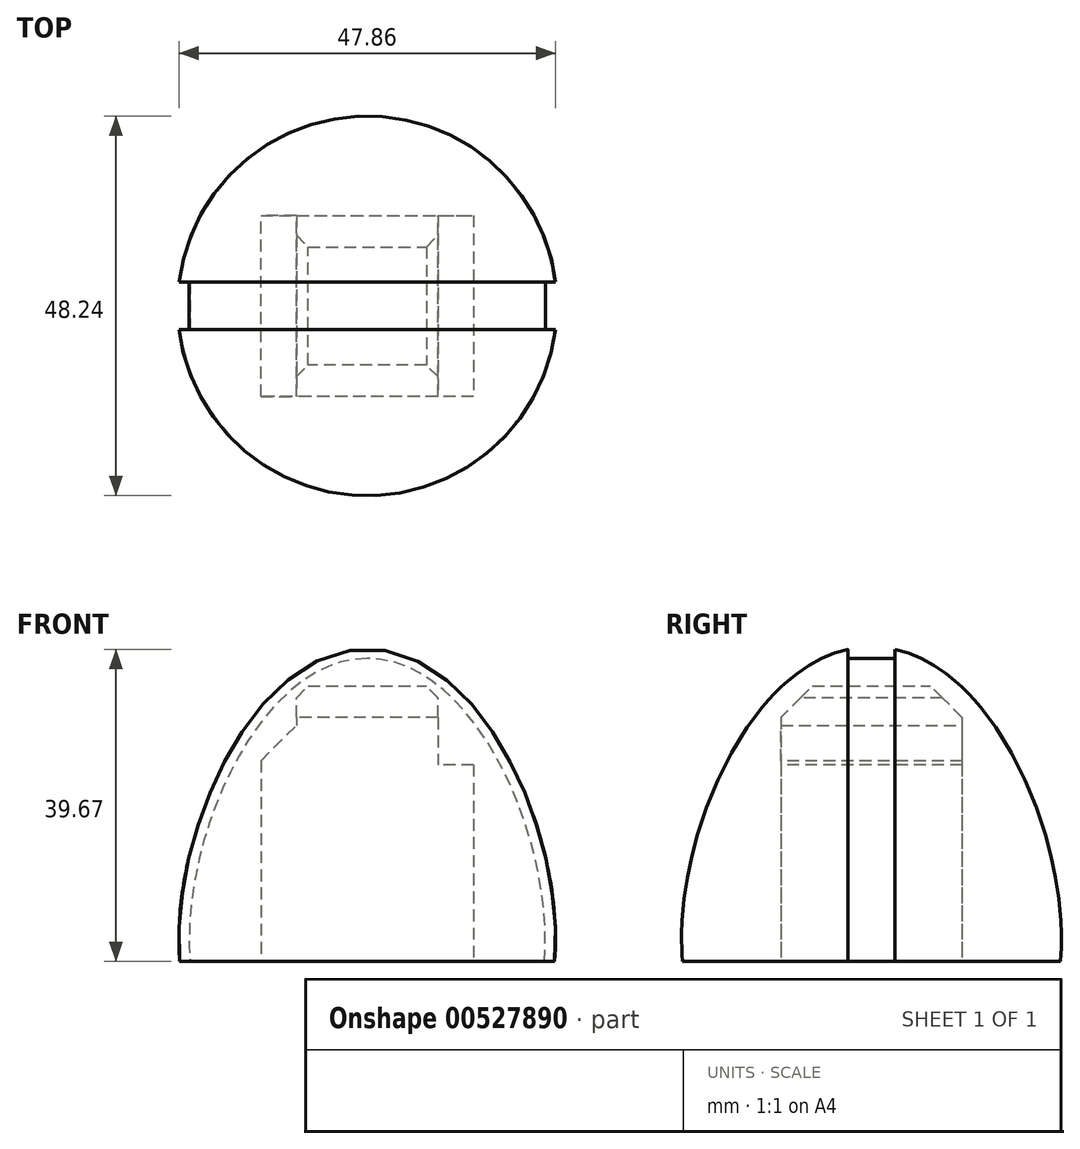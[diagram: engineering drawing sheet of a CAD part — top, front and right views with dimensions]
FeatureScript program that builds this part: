
annotation { "Feature Type Name" : "Feature", "Feature Type Description" : "" }
export const myFeature = defineFeature(function(context is Context, id is Id, definition is map)
    precondition{}
    {
        {
            var Q0;
            Q0=qCreatedBy(makeId("Front.planeOp"),FACE);
            var sketch = newSketch(context, id + "F0", { "sketchPlane" : qUnion([Q0])});
            skLineSegment(sketch, "E0", {"start": v(0, 0) * mm, "end": v(0, 60) * mm});
            skLineSegment(sketch, "E1", {"start": v(0, 0) * mm, "end": v(0, 20) * mm, "construction": true});
            skLineSegment(sketch, "E2", {"start": v(0, 20) * mm, "end": v(24, 20) * mm});
            skLineSegment(sketch, "E3", {"start": v(0, 60) * mm, "end": v(15, 60) * mm, "construction": true});
            skLineSegment(sketch, "E4", {"start": v(0, 0) * mm, "end": v(14, 0) * mm, "construction": true});
            skFitSpline(sketch, "E5", {"points": [v(0, 0) * mm, v(24, 20) * mm, v(0, 60) * mm], "startDerivative": vector(93.32, 0) * mm, "endDerivative": vector(-81.83, 0) * mm});
            skFitSpline(sketch, "E6.MirrorCS", {"points": [v(0, 0) * mm, v(-24, 20) * mm, v(0, 60) * mm], "startDerivative": vector(-93.32, 0) * mm, "endDerivative": vector(81.83, 0) * mm});
            skSolve(sketch);
        }
        {
            var Q0;
            {var subQ3=sQuery(id+"F0.wireOp",EDGE,"E2");Q0=makeQuery(id+"F0.imprint","IMPRINT",FACE,{"disambiguationData":[TD([[makeQuery(id+"F0.imprint","IMPRINT",EDGE,{"derivedFrom":subQ3}),1.0]])]});}
            var Q1;
            Q1=sQuery(id+"F0.wireOp",EDGE,"E0");
            revolve(context, id + "F1", {"entities" : qUnion([Q0]), "axis" : qUnion([Q1]), "revolveType" : RevolveType.FULL});
        }
        {
            var Q0;
            Q0=makeQuery(id+"F1.opRevolve","SWEPT_FACE",FACE,{"disambiguationData":[OSD([sQuery(id+"F0.wireOp",EDGE,"E2")])]});
            var sketch = newSketch(context, id + "F2", { "sketchPlane" : qUnion([Q0])});
            skLineSegment(sketch, "E7", {"start": v(0, 0) * mm, "end": v(13.5, 0) * mm});
            skLineSegment(sketch, "E8", {"start": v(13.5, 0) * mm, "end": v(13.5, 11.5) * mm});
            skLineSegment(sketch, "E9", {"start": v(13.5, 11.5) * mm, "end": v(-13.5, 11.5) * mm});
            skLineSegment(sketch, "E10", {"start": v(-13.5, 11.5) * mm, "end": v(-13.5, -11.5) * mm});
            skLineSegment(sketch, "E11", {"start": v(-13.5, -11.5) * mm, "end": v(13.5, -11.5) * mm});
            skLineSegment(sketch, "E12", {"start": v(13.5, -11.5) * mm, "end": v(13.5, 0) * mm});
            skSolve(sketch);
        }
        {
            var Q0;
            Q0=qSketchRegion(id+"F2",true);
            extrude(context, id + "F3", {"entities" : qUnion([Q0]), "operationType" : NewBodyOperationType.REMOVE, "oppositeDirection" : true, "depth" : 25 * mm});
        }
        {
            var Q0;
            Q0=makeQuery(id+"F3.boolean.opBoolean","COPY",FACE,{"derivedFrom":makeQuery(id+"F3.opExtrude","CAP_FACE",FACE,{"disambiguationData":[OSD([sQuery(id+"F2.wireOp",EDGE,"E8"),sQuery(id+"F2.wireOp",EDGE,"E9"),sQuery(id+"F2.wireOp",EDGE,"E10"),sQuery(id+"F2.wireOp",EDGE,"E11"),sQuery(id+"F2.wireOp",EDGE,"E12")])],"isStart":false})});
            var sketch = newSketch(context, id + "F4", { "sketchPlane" : qUnion([Q0])});
            skLineSegment(sketch, "E13", {"start": v(0, 0) * mm, "end": v(5, 0) * mm, "construction": true});
            skLineSegment(sketch, "E14", {"start": v(5, 0) * mm, "end": v(5, 5) * mm});
            skLineSegment(sketch, "E15", {"start": v(5, 5) * mm, "end": v(-5, 5) * mm});
            skLineSegment(sketch, "E16", {"start": v(-5, 5) * mm, "end": v(-5, -5) * mm});
            skLineSegment(sketch, "E17", {"start": v(-5, -5) * mm, "end": v(5, -5) * mm});
            skLineSegment(sketch, "E18", {"start": v(5, -5) * mm, "end": v(5, 0) * mm});
            skSolve(sketch);
        }
        {
            var Q0;
            Q0=qSketchRegion(id+"F4",true);
            extrude(context, id + "F5", {"entities" : qUnion([Q0]), "operationType" : NewBodyOperationType.REMOVE, "oppositeDirection" : true, "depth" : 10 * mm});
        }
        {
            var Q0;
            Q0=makeQuery(id+"F3.boolean.opBoolean","COPY",FACE,{"derivedFrom":makeQuery(id+"F3.opExtrude","CAP_FACE",FACE,{"disambiguationData":[OSD([sQuery(id+"F2.wireOp",EDGE,"E8"),sQuery(id+"F2.wireOp",EDGE,"E9"),sQuery(id+"F2.wireOp",EDGE,"E10"),sQuery(id+"F2.wireOp",EDGE,"E11"),sQuery(id+"F2.wireOp",EDGE,"E12")])],"isStart":false})});
            var sketch = newSketch(context, id + "F6", { "sketchPlane" : qUnion([Q0])});
            skLineSegment(sketch, "E19", {"start": v(0, 0) * mm, "end": v(9, 0) * mm, "construction": true});
            skLineSegment(sketch, "E20", {"start": v(9, 0) * mm, "end": v(9, 11.5) * mm});
            skLineSegment(sketch, "E21", {"start": v(9, 11.5) * mm, "end": v(-9, 11.5) * mm});
            skLineSegment(sketch, "E22", {"start": v(-9, 11.5) * mm, "end": v(-9, -11.5) * mm});
            skLineSegment(sketch, "E23", {"start": v(-9, -11.5) * mm, "end": v(9, -11.5) * mm});
            skLineSegment(sketch, "E24", {"start": v(9, -11.5) * mm, "end": v(9, 0) * mm});
            skSolve(sketch);
        }
        {
            var Q0;
            Q0=qSketchRegion(id+"F6",true);
            extrude(context, id + "F7", {"entities" : qUnion([Q0]), "operationType" : NewBodyOperationType.REMOVE, "oppositeDirection" : true, "depth" : 6 * mm});
        }
        {
            var Q0;
            Q0=makeQuery(id+"F7.boolean.opBoolean","COPY",EDGE,{"derivedFrom":makeQuery(id+"F7.opExtrude","CAP_EDGE",EDGE,{"disambiguationData":[OSD([sQuery(id+"F6.wireOp",EDGE,"E22")])],"isStart":true})});
            var Q1;
            Q1=makeQuery(id+"F7.boolean.opBoolean","COPY",EDGE,{"derivedFrom":makeQuery(id+"F7.opExtrude","CAP_EDGE",EDGE,{"disambiguationData":[OSD([sQuery(id+"F6.wireOp",EDGE,"E20"),sQuery(id+"F6.wireOp",EDGE,"E24")])],"isStart":true})});
            chamfer(context, id + "F8", {"entities" : qUnion([Q0, Q1]), "width" : 5 * mm, "tangentPropagation" : true});
        }
        {
            var Q0;
            Q0=makeQuery(id+"F7.boolean.opBoolean","INTERSECT",EDGE,{"derivedFrom":[makeQuery(id+"F5.boolean.opBoolean","COPY",FACE,{"derivedFrom":makeQuery(id+"F5.opExtrude","SWEPT_FACE",FACE,{"disambiguationData":[OSD([sQuery(id+"F4.wireOp",EDGE,"E16")])]})}),makeQuery(id+"F7.opExtrude","CAP_FACE",FACE,{"disambiguationData":[OSD([sQuery(id+"F6.wireOp",EDGE,"E20"),sQuery(id+"F6.wireOp",EDGE,"E21"),sQuery(id+"F6.wireOp",EDGE,"E22"),sQuery(id+"F6.wireOp",EDGE,"E23"),sQuery(id+"F6.wireOp",EDGE,"E24")])],"isStart":false})]});
            var Q1;
            Q1=makeQuery(id+"F7.boolean.opBoolean","INTERSECT",EDGE,{"derivedFrom":[makeQuery(id+"F5.boolean.opBoolean","COPY",FACE,{"derivedFrom":makeQuery(id+"F5.opExtrude","SWEPT_FACE",FACE,{"disambiguationData":[OSD([sQuery(id+"F4.wireOp",EDGE,"E15")])]})}),makeQuery(id+"F7.opExtrude","CAP_FACE",FACE,{"disambiguationData":[OSD([sQuery(id+"F6.wireOp",EDGE,"E20"),sQuery(id+"F6.wireOp",EDGE,"E21"),sQuery(id+"F6.wireOp",EDGE,"E22"),sQuery(id+"F6.wireOp",EDGE,"E23"),sQuery(id+"F6.wireOp",EDGE,"E24")])],"isStart":false})]});
            var Q2;
            Q2=makeQuery(id+"F7.boolean.opBoolean","INTERSECT",EDGE,{"derivedFrom":[makeQuery(id+"F5.boolean.opBoolean","COPY",FACE,{"derivedFrom":makeQuery(id+"F5.opExtrude","SWEPT_FACE",FACE,{"disambiguationData":[OSD([sQuery(id+"F4.wireOp",EDGE,"E14"),sQuery(id+"F4.wireOp",EDGE,"E18")])]})}),makeQuery(id+"F7.opExtrude","CAP_FACE",FACE,{"disambiguationData":[OSD([sQuery(id+"F6.wireOp",EDGE,"E20"),sQuery(id+"F6.wireOp",EDGE,"E21"),sQuery(id+"F6.wireOp",EDGE,"E22"),sQuery(id+"F6.wireOp",EDGE,"E23"),sQuery(id+"F6.wireOp",EDGE,"E24")])],"isStart":false})]});
            var Q3;
            Q3=makeQuery(id+"F7.boolean.opBoolean","INTERSECT",EDGE,{"derivedFrom":[makeQuery(id+"F5.boolean.opBoolean","COPY",FACE,{"derivedFrom":makeQuery(id+"F5.opExtrude","SWEPT_FACE",FACE,{"disambiguationData":[OSD([sQuery(id+"F4.wireOp",EDGE,"E17")])]})}),makeQuery(id+"F7.opExtrude","CAP_FACE",FACE,{"disambiguationData":[OSD([sQuery(id+"F6.wireOp",EDGE,"E20"),sQuery(id+"F6.wireOp",EDGE,"E21"),sQuery(id+"F6.wireOp",EDGE,"E22"),sQuery(id+"F6.wireOp",EDGE,"E23"),sQuery(id+"F6.wireOp",EDGE,"E24")])],"isStart":false})]});
            chamfer(context, id + "F9", {"entities" : qUnion([Q0, Q1, Q2, Q3]), "width" : 6.5 * mm, "tangentPropagation" : true});
        }
        {
            var Q0;
            Q0=qCreatedBy(makeId("Right.planeOp"),FACE);
            var sketch = newSketch(context, id + "F10", { "sketchPlane" : qUnion([Q0])});
            skLineSegment(sketch, "E25", {"start": v(0, 0) * mm, "end": v(3, 0) * mm});
            skLineSegment(sketch, "E26", {"start": v(3, 0) * mm, "end": v(3, 1.5) * mm});
            skLineSegment(sketch, "E27", {"start": v(3, 1.5) * mm, "end": v(-3, 1.5) * mm});
            skLineSegment(sketch, "E28", {"start": v(-3, 1.5) * mm, "end": v(-3, 0) * mm});
            skLineSegment(sketch, "E29", {"start": v(-3, 0) * mm, "end": v(0, 0) * mm});
            skSolve(sketch);
        }
        {
            var Q0;
            Q0=makeQuery(id+"F10.imprint","IMPRINT",FACE,{"disambiguationData":[TD([[makeQuery(id+"F10.imprint","IMPRINT",EDGE,{"derivedFrom":sQuery(id+"F10.wireOp",EDGE,"E25")}),1.0]])]});
            var Q1;
            Q1=sQuery(id+"F0.wireOp",EDGE,"E5");
            var Q2;
            Q2=sQuery(id+"F0.wireOp",EDGE,"E6.MirrorCS");
            sweep(context, id + "F11", {"operationType" : NewBodyOperationType.REMOVE, "profiles" : qUnion([Q0]), "path" : qUnion([Q1, Q2])});
        }
    });
